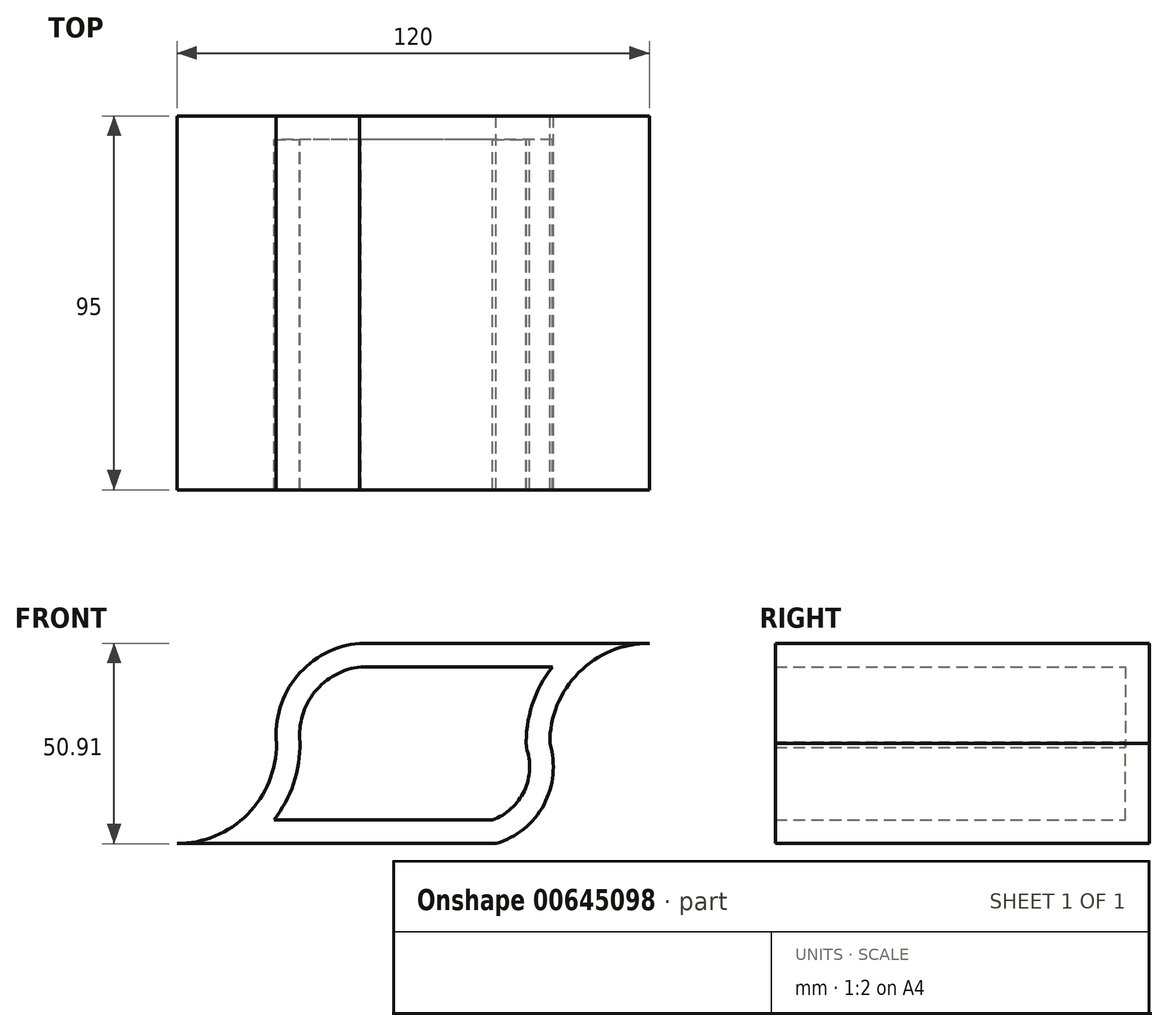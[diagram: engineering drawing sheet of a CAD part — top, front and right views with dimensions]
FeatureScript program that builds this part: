
annotation { "Feature Type Name" : "Feature", "Feature Type Description" : "" }
export const myFeature = defineFeature(function(context is Context, id is Id, definition is map)
    precondition{}
    {
        {
            var Q0;
            Q0=qCreatedBy(makeId("Front.planeOp"),FACE);
            var sketch = newSketch(context, id + "F0", { "sketchPlane" : qUnion([Q0])});
            skLineSegment(sketch, "E0.bottom", {"start": v(58.38, -21.5) * mm, "end": v(-61.62, -21.5) * mm});
            skLineSegment(sketch, "E0.top", {"start": v(58.38, 29.4) * mm, "end": v(-61.62, 29.4) * mm});
            skLineSegment(sketch, "E0.left", {"start": v(58.38, -21.5) * mm, "end": v(58.38, 29.4) * mm});
            skLineSegment(sketch, "E0.right", {"start": v(-61.62, -21.5) * mm, "end": v(-61.62, 29.4) * mm});
            skLineSegment(sketch, "E1", {"start": v(-61.62, 3.95) * mm, "end": v(58.38, 3.95) * mm});
            skArc(sketch, "E2", {"start": v(-61.62, -21.5) * mm, "mid": v(-43.69, -14.04) * mm, "end": v(-36.35, 3.95) * mm});
            skArc(sketch, "E3", {"start": v(-11.08, 29.4) * mm, "mid": v(-29.68, 22.6) * mm, "end": v(-36.35, 3.95) * mm});
            skArc(sketch, "E4", {"start": v(58.38, 29.4) * mm, "mid": v(40.44, 21.94) * mm, "end": v(33.1, 3.95) * mm});
            skArc(sketch, "E5", {"start": v(7.83, -21.5) * mm, "mid": v(28.08, -16.34) * mm, "end": v(33.1, 3.95) * mm});
            skSolve(sketch);
        }
        {
            var Q0;
            {var subQ6=sQuery(id+"F0.wireOp",EDGE,"E4");Q0=makeQuery(id+"F0.imprint","IMPRINT",FACE,{"disambiguationData":[TD([[makeQuery(id+"F0.imprint","IMPRINT",EDGE,{"derivedFrom":subQ6}),-1.0]])]});}
            var Q1;
            {var subQ0=sQuery(id+"F0.wireOp",EDGE,"E2");Q1=makeQuery(id+"F0.imprint","IMPRINT",FACE,{"disambiguationData":[TD([[makeQuery(id+"F0.imprint","IMPRINT",EDGE,{"derivedFrom":subQ0}),-1.0]])]});}
            extrude(context, id + "F1", {"entities" : qUnion([Q0, Q1]), "depth" : 95 * mm, "offsetDistance" : 25 * mm});
        }
        {
            var Q0;
            Q0=makeQuery(id+"F1.opExtrude","CAP_FACE",FACE,{"disambiguationData":[OSD([sQuery(id+"F0.wireOp",EDGE,"E0.bottom"),sQuery(id+"F0.wireOp",EDGE,"E0.top"),sQuery(id+"F0.wireOp",EDGE,"E2"),sQuery(id+"F0.wireOp",EDGE,"E3"),sQuery(id+"F0.wireOp",EDGE,"E4"),sQuery(id+"F0.wireOp",EDGE,"E5")])],"isStart":false});
            shell(context, id + "F2", {"entities" : qUnion([Q0]), "thickness" : 6 * mm});
        }
    });
